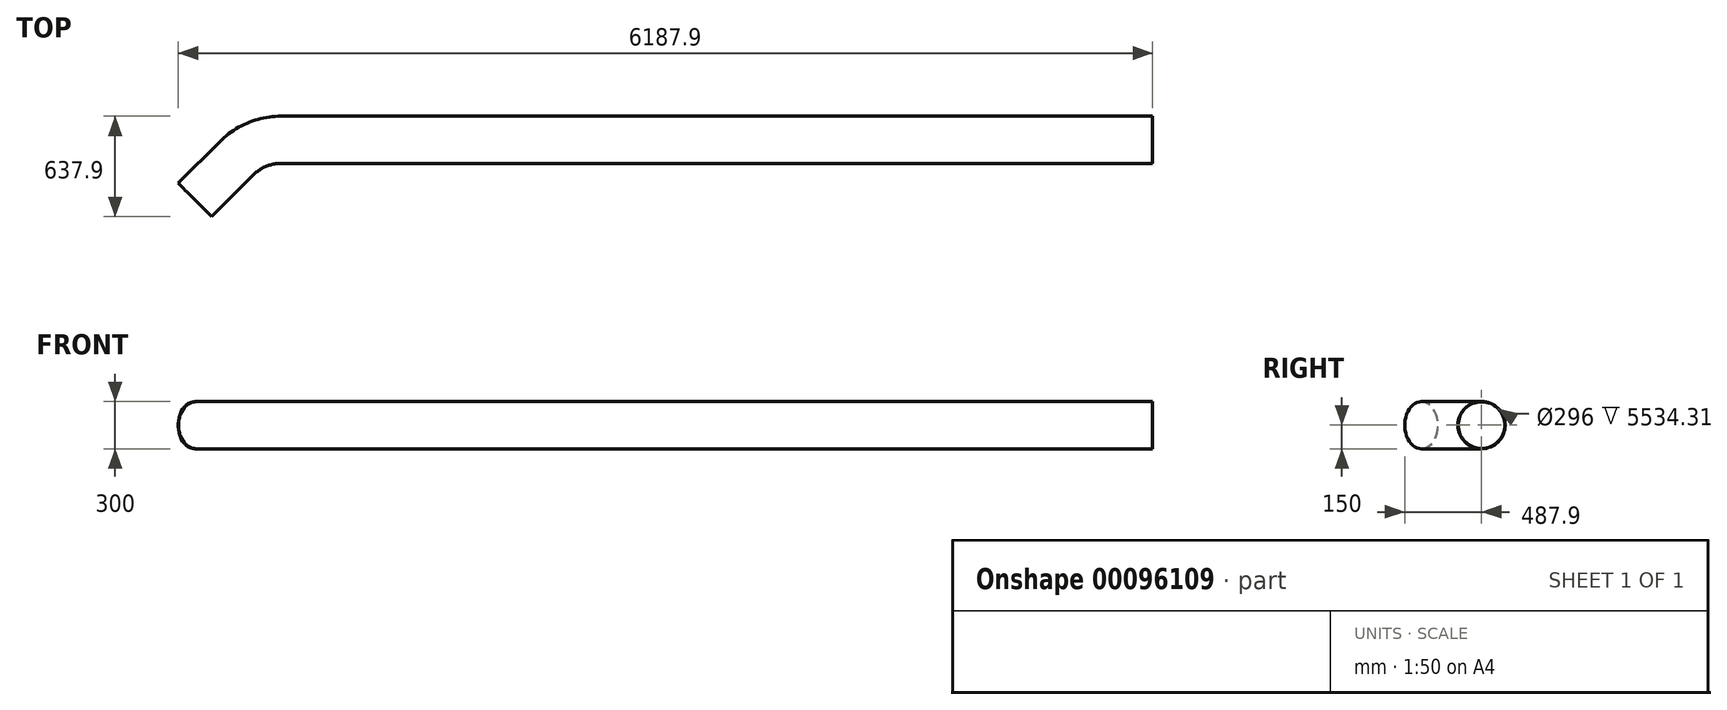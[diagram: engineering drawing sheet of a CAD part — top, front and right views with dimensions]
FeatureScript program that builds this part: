
annotation { "Feature Type Name" : "Feature", "Feature Type Description" : "" }
export const myFeature = defineFeature(function(context is Context, id is Id, definition is map)
    precondition{}
    {
        {
            var Q0;
            Q0=qCreatedBy(makeId("Right.planeOp"),FACE);
            var sketch = newSketch(context, id + "F0", { "sketchPlane" : qUnion([Q0])});
            skCircle(sketch, "E0", {"center": v(0, 0) * mm, "radius": 150 * mm});
            skCircle(sketch, "E1", {"center": v(0, 0) * mm, "radius": 148 * mm});
            skSolve(sketch);
        }
        {
            var Q0;
            Q0=qCreatedBy(makeId("Top.planeOp"),FACE);
            var sketch = newSketch(context, id + "F1", { "sketchPlane" : qUnion([Q0])});
            skLineSegment(sketch, "E2", {"start": v(0, 0) * mm, "end": v(-5534.31, 0) * mm});
            skLineSegment(sketch, "E3", {"start": v(-5817.16, -117.16) * mm, "end": v(-6081.84, -381.84) * mm});
            skPoint(sketch, "E4.visualSharp", {"position": v(-5700, 0) * mm});
            skArc(sketch, "E4.filletArc", {"start": v(-5534.31, 0) * mm, "mid": v(-5687.39, -30.45) * mm, "end": v(-5817.16, -117.16) * mm});
            skSolve(sketch);
        }
        {
            var Q0;
            Q0=makeQuery(id+"F0.imprint","IMPRINT",FACE,{"disambiguationData":[TD([[makeQuery(id+"F0.imprint","IMPRINT",EDGE,{"derivedFrom":sQuery(id+"F0.wireOp",EDGE,"E0")}),1.0]])]});
            var Q1;
            Q1=sQuery(id+"F1.wireOp",EDGE,"E2");
            var Q2;
            Q2=sQuery(id+"F1.wireOp",EDGE,"E4.filletArc");
            var Q3;
            Q3=sQuery(id+"F1.wireOp",EDGE,"E3");
            sweep(context, id + "F2", {"profiles" : qUnion([Q0]), "path" : qUnion([Q1, Q2, Q3])});
        }
    });
